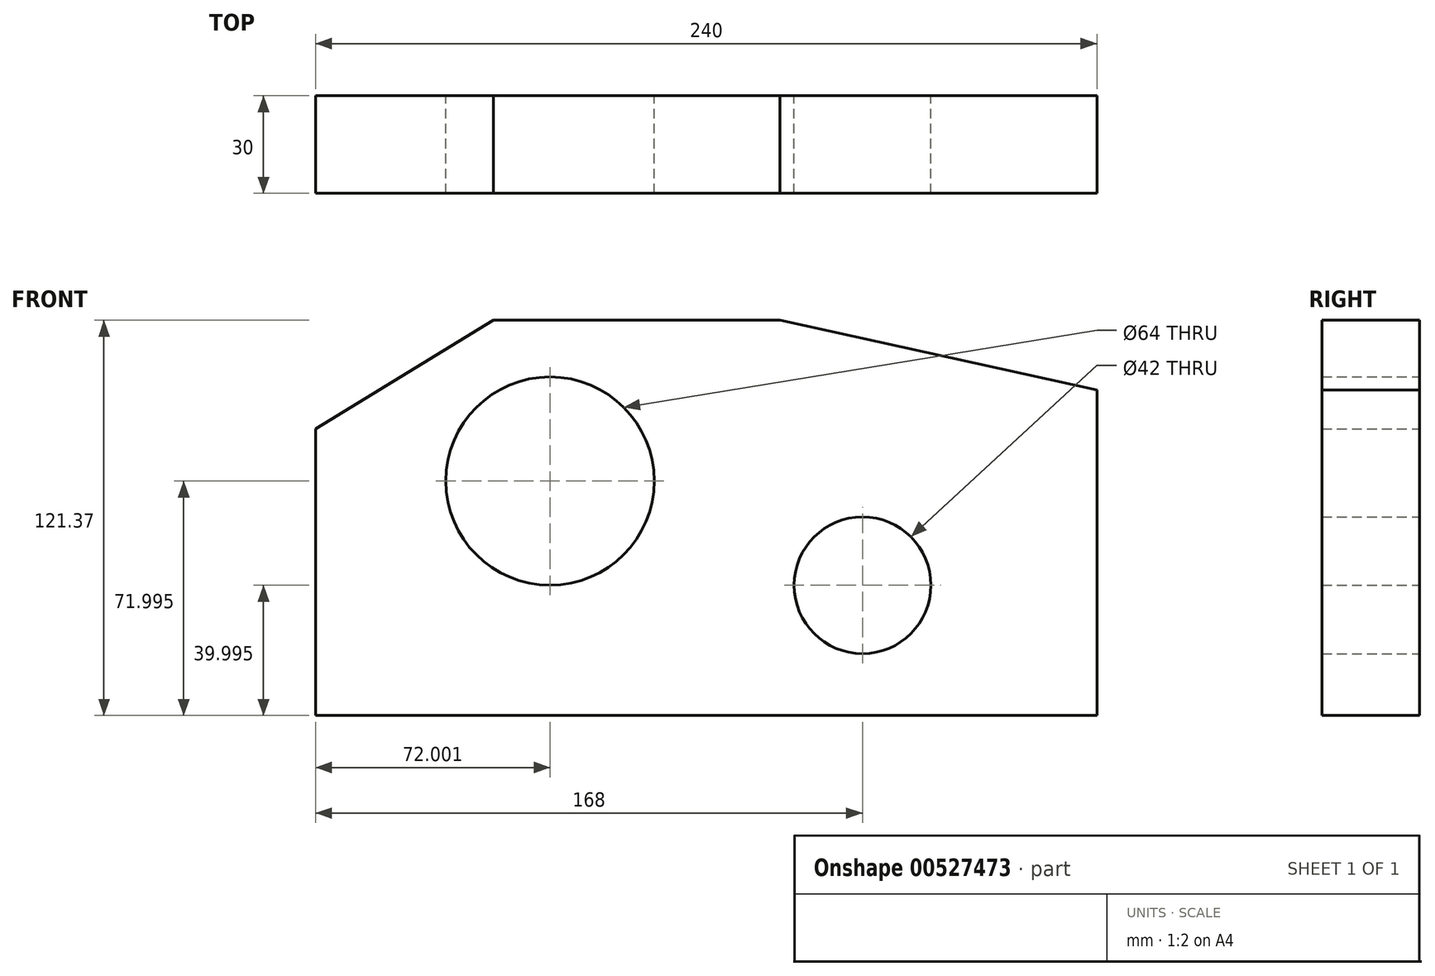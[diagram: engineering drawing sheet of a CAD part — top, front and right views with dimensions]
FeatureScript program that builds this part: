
annotation { "Feature Type Name" : "Feature", "Feature Type Description" : "" }
export const myFeature = defineFeature(function(context is Context, id is Id, definition is map)
    precondition{}
    {
        {
            var Q0;
            Q0=qCreatedBy(makeId("Front.planeOp"),FACE);
            var sketch = newSketch(context, id + "F0", { "sketchPlane" : qUnion([Q0])});
            skLineSegment(sketch, "E0", {"start": v(-119.98, -49.51) * mm, "end": v(120.02, -49.51) * mm});
            skLineSegment(sketch, "E1", {"start": v(120.02, -49.51) * mm, "end": v(120.02, 50.49) * mm});
            skLineSegment(sketch, "E2", {"start": v(-119.98, -49.51) * mm, "end": v(-119.98, 38.49) * mm});
            skLineSegment(sketch, "E3", {"start": v(-119.98, 38.49) * mm, "end": v(-65.37, 71.86) * mm});
            skLineSegment(sketch, "E4", {"start": v(-65.37, 71.86) * mm, "end": v(22.63, 71.86) * mm});
            skLineSegment(sketch, "E5", {"start": v(22.63, 71.86) * mm, "end": v(120.02, 50.49) * mm});
            skCircle(sketch, "E6", {"center": v(-47.98, 22.49) * mm, "radius": 32 * mm});
            skCircle(sketch, "E7", {"center": v(48.02, -9.51) * mm, "radius": 21 * mm});
            skSolve(sketch);
        }
        {
            var Q0;
            Q0=makeQuery(id+"F0.imprint","IMPRINT",FACE,{"disambiguationData":[TD([[makeQuery(id+"F0.imprint","IMPRINT",EDGE,{"derivedFrom":sQuery(id+"F0.wireOp",EDGE,"E0")}),1.0]])]});
            extrude(context, id + "F1", {"entities" : qUnion([Q0]), "depth" : 30 * mm, "offsetDistance" : 25 * mm});
        }
    });
